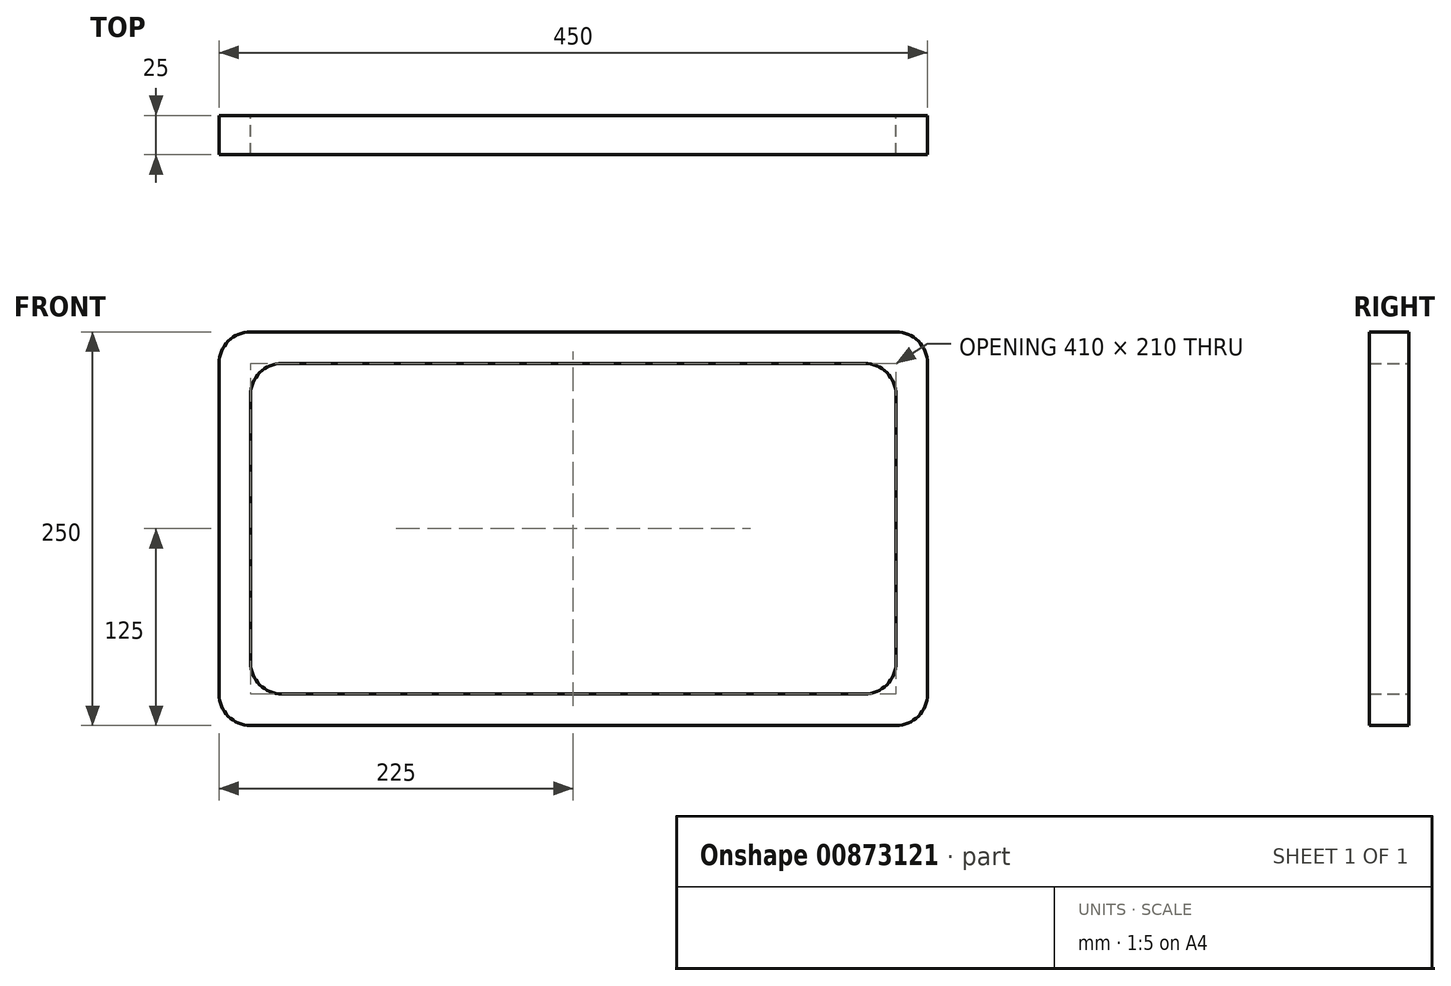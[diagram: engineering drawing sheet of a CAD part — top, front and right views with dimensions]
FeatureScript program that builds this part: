
annotation { "Feature Type Name" : "Feature", "Feature Type Description" : "" }
export const myFeature = defineFeature(function(context is Context, id is Id, definition is map)
    precondition{}
    {
        {
            var Q0;
            Q0=qCreatedBy(makeId("Front.planeOp"),FACE);
            var sketch = newSketch(context, id + "F0", { "sketchPlane" : qUnion([Q0])});
            skLineSegment(sketch, "E0.bottom", {"start": v(225, -125) * mm, "end": v(-225, -125) * mm});
            skLineSegment(sketch, "E0.top", {"start": v(225, 125) * mm, "end": v(-225, 125) * mm});
            skLineSegment(sketch, "E0.left", {"start": v(225, -125) * mm, "end": v(225, 125) * mm});
            skLineSegment(sketch, "E0.right", {"start": v(-225, -125) * mm, "end": v(-225, 125) * mm});
            skPoint(sketch, "E0.middle", {"position": v(0, 0) * mm});
            skLineSegment(sketch, "E1.bottom", {"start": v(205, -105) * mm, "end": v(-205, -105) * mm});
            skLineSegment(sketch, "E1.top", {"start": v(205, 105) * mm, "end": v(-205, 105) * mm});
            skLineSegment(sketch, "E1.left", {"start": v(205, -105) * mm, "end": v(205, 105) * mm});
            skLineSegment(sketch, "E1.right", {"start": v(-205, -105) * mm, "end": v(-205, 105) * mm});
            skSolve(sketch);
        }
        {
            var Q0;
            Q0=makeQuery(id+"F0.imprint","IMPRINT",FACE,{"disambiguationData":[TD([[makeQuery(id+"F0.imprint","IMPRINT",EDGE,{"derivedFrom":sQuery(id+"F0.wireOp",EDGE,"E0.bottom")}),-1.0]])]});
            extrude(context, id + "F1", {"entities" : qUnion([Q0]), "depth" : 25 * mm, "offsetDistance" : 25 * mm});
        }
        {
            var Q0;
            Q0=makeQuery(id+"F1.opExtrude","SWEPT_EDGE",EDGE,{"disambiguationData":[OSD([sQuery(id+"F0.wireOp",EDGE,"E1.top"),sQuery(id+"F0.wireOp",EDGE,"E1.right")])]});
            var Q1;
            Q1=makeQuery(id+"F1.opExtrude","SWEPT_EDGE",EDGE,{"disambiguationData":[OSD([sQuery(id+"F0.wireOp",EDGE,"E1.top"),sQuery(id+"F0.wireOp",EDGE,"E1.left")])]});
            var Q2;
            Q2=makeQuery(id+"F1.opExtrude","SWEPT_EDGE",EDGE,{"disambiguationData":[OSD([sQuery(id+"F0.wireOp",EDGE,"E1.bottom"),sQuery(id+"F0.wireOp",EDGE,"E1.left")])]});
            var Q3;
            Q3=makeQuery(id+"F1.opExtrude","SWEPT_EDGE",EDGE,{"disambiguationData":[OSD([sQuery(id+"F0.wireOp",EDGE,"E1.bottom"),sQuery(id+"F0.wireOp",EDGE,"E1.right")])]});
            var Q4;
            Q4=makeQuery(id+"F1.opExtrude","SWEPT_EDGE",EDGE,{"disambiguationData":[OSD([sQuery(id+"F0.wireOp",EDGE,"E0.top"),sQuery(id+"F0.wireOp",EDGE,"E0.right")])]});
            var Q5;
            Q5=makeQuery(id+"F1.opExtrude","SWEPT_EDGE",EDGE,{"disambiguationData":[OSD([sQuery(id+"F0.wireOp",EDGE,"E0.top"),sQuery(id+"F0.wireOp",EDGE,"E0.left")])]});
            var Q6;
            Q6=makeQuery(id+"F1.opExtrude","SWEPT_EDGE",EDGE,{"disambiguationData":[OSD([sQuery(id+"F0.wireOp",EDGE,"E0.bottom"),sQuery(id+"F0.wireOp",EDGE,"E0.left")])]});
            var Q7;
            Q7=makeQuery(id+"F1.opExtrude","SWEPT_EDGE",EDGE,{"disambiguationData":[OSD([sQuery(id+"F0.wireOp",EDGE,"E0.bottom"),sQuery(id+"F0.wireOp",EDGE,"E0.right")])]});
            fillet(context, id + "F2", {"entities" : qUnion([Q0, Q1, Q2, Q3, Q4, Q5, Q6, Q7]), "radius" : 20 * mm, "tangentPropagation" : true, "allowEdgeOverflow" : false});
        }
    });
